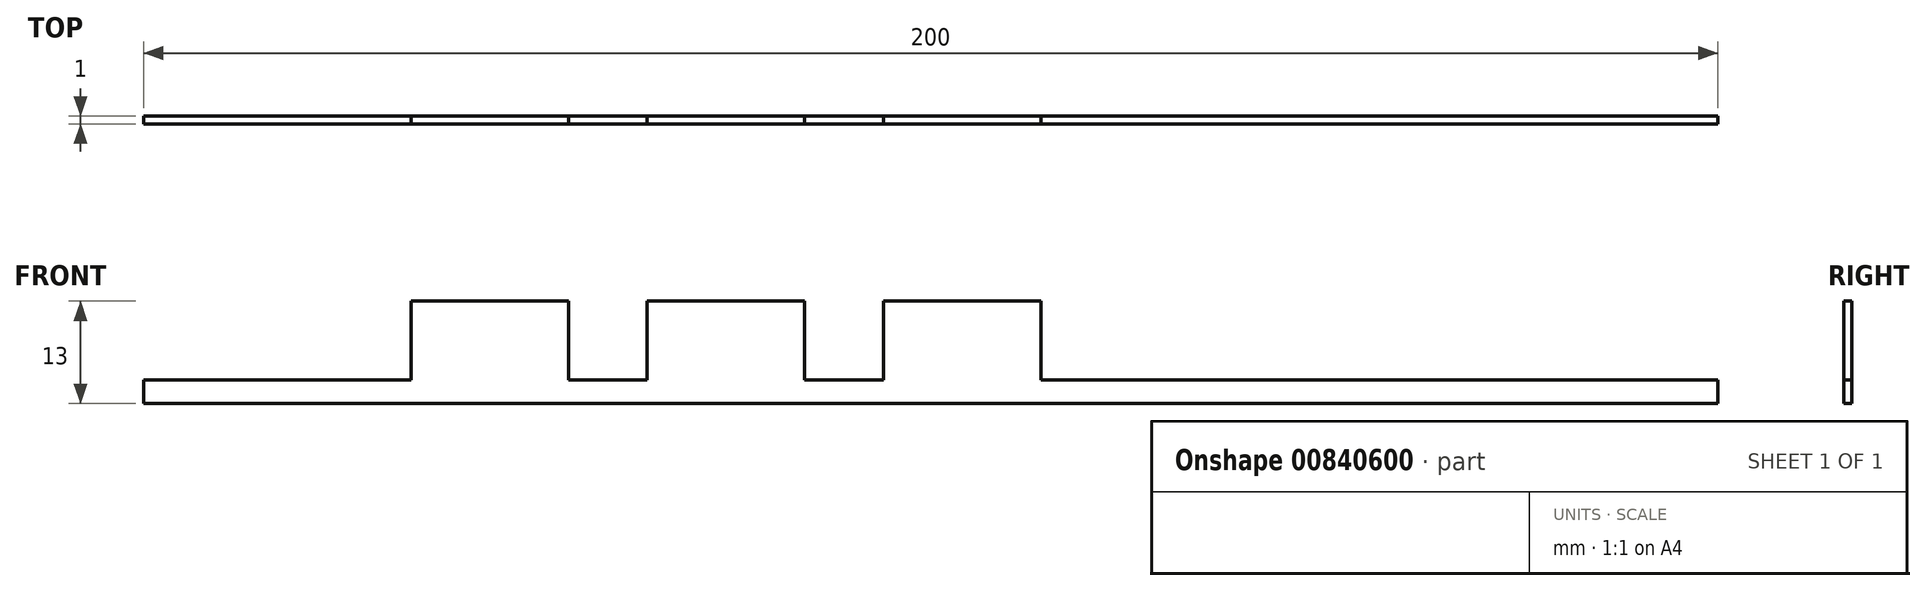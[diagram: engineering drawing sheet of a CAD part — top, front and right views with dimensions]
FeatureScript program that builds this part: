
annotation { "Feature Type Name" : "Feature", "Feature Type Description" : "" }
export const myFeature = defineFeature(function(context is Context, id is Id, definition is map)
    precondition{}
    {
        {
            var Q0;
            Q0=qCreatedBy(makeId("Front.planeOp"),FACE);
            var sketch = newSketch(context, id + "F0", { "sketchPlane" : qUnion([Q0])});
            skLineSegment(sketch, "E0.bottom", {"start": v(0, 18) * mm, "end": v(200, 18) * mm});
            skLineSegment(sketch, "E0.top", {"start": v(0, 21) * mm, "end": v(200, 21) * mm});
            skLineSegment(sketch, "E0.left", {"start": v(0, 18) * mm, "end": v(0, 21) * mm});
            skLineSegment(sketch, "E0.right", {"start": v(200, 18) * mm, "end": v(200, 21) * mm});
            skLineSegment(sketch, "E1.bottom", {"start": v(34, 21) * mm, "end": v(54, 21) * mm});
            skLineSegment(sketch, "E1.top", {"start": v(34, 31) * mm, "end": v(54, 31) * mm});
            skLineSegment(sketch, "E1.left", {"start": v(34, 21) * mm, "end": v(34, 31) * mm});
            skLineSegment(sketch, "E1.right", {"start": v(54, 21) * mm, "end": v(54, 31) * mm});
            skLineSegment(sketch, "E2.bottom", {"start": v(64, 21) * mm, "end": v(84, 21) * mm});
            skLineSegment(sketch, "E2.top", {"start": v(64, 31) * mm, "end": v(84, 31) * mm});
            skLineSegment(sketch, "E2.left", {"start": v(64, 21) * mm, "end": v(64, 31) * mm});
            skLineSegment(sketch, "E2.right", {"start": v(84, 21) * mm, "end": v(84, 31) * mm});
            skLineSegment(sketch, "E3.bottom", {"start": v(94, 21) * mm, "end": v(114, 21) * mm});
            skLineSegment(sketch, "E3.top", {"start": v(94, 31) * mm, "end": v(114, 31) * mm});
            skLineSegment(sketch, "E3.left", {"start": v(94, 21) * mm, "end": v(94, 31) * mm});
            skLineSegment(sketch, "E3.right", {"start": v(114, 21) * mm, "end": v(114, 31) * mm});
            skSolve(sketch);
        }
        {
            var Q0;
            Q0 = qSketchRegion(id + "F0", true);
            extrude(context, id + "F1", {"entities" : qUnion([Q0]), "depth" : 1 * mm, "offsetDistance" : 25 * mm});
        }
    });
